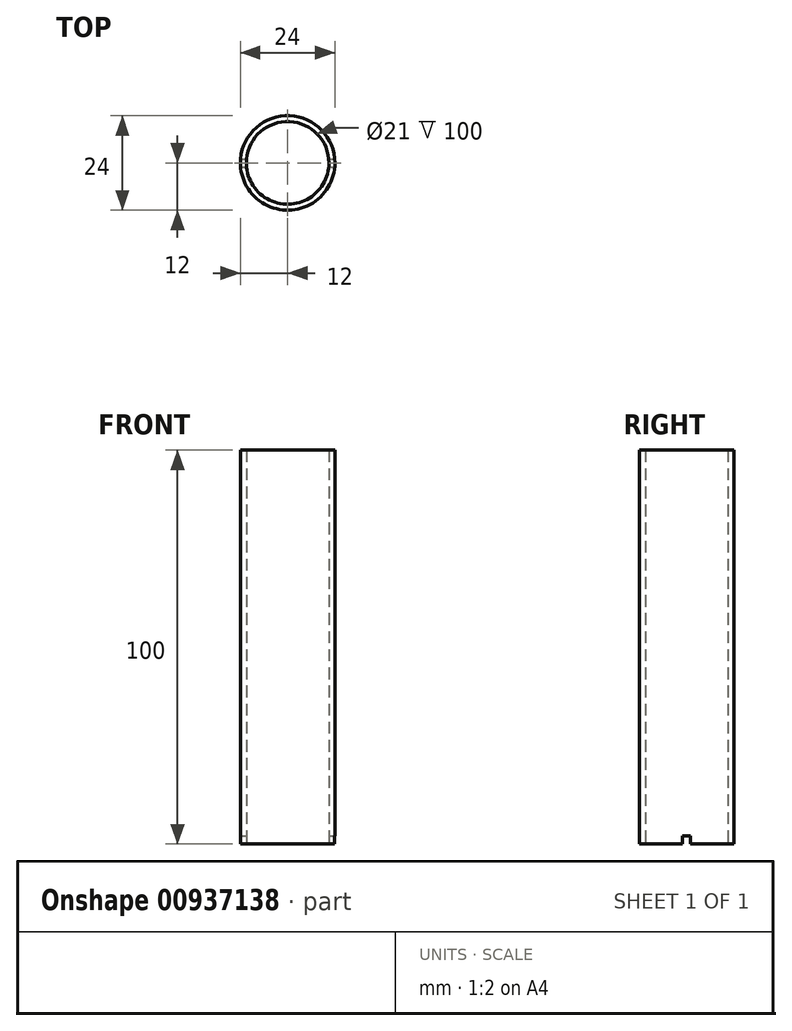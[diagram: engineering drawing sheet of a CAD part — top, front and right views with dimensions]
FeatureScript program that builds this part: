
annotation { "Feature Type Name" : "Feature", "Feature Type Description" : "" }
export const myFeature = defineFeature(function(context is Context, id is Id, definition is map)
    precondition{}
    {
        {
            var Q0;
            Q0=qCreatedBy(makeId("Top.planeOp"),FACE);
            var sketch = newSketch(context, id + "F0", { "sketchPlane" : qUnion([Q0])});
            skCircle(sketch, "E0", {"center": v(0, 0) * mm, "radius": 12 * mm});
            skCircle(sketch, "E1", {"center": v(0, 0) * mm, "radius": 10.5 * mm});
            skSolve(sketch);
        }
        {
            var Q0;
            Q0 = qSketchRegion(id + "F0", true);
            extrude(context, id + "F1", {"entities" : qUnion([Q0]), "depth" : 100 * mm, "offsetDistance" : 25 * mm});
        }
        {
            var Q0;
            Q0=qCreatedBy(makeId("Right.planeOp"),FACE);
            var sketch = newSketch(context, id + "F2", { "sketchPlane" : qUnion([Q0])});
            skLineSegment(sketch, "E2", {"start": v(-1, 0) * mm, "end": v(-1, 2) * mm});
            skLineSegment(sketch, "E3", {"start": v(-1, 2) * mm, "end": v(1, 2) * mm});
            skLineSegment(sketch, "E4", {"start": v(1, 2) * mm, "end": v(1, 0) * mm});
            skLineSegment(sketch, "E5", {"start": v(1, 0) * mm, "end": v(-1, 0) * mm});
            skSolve(sketch);
        }
        {
            var Q0;
            Q0 = qSketchRegion(id + "F2", true);
            extrude(context, id + "F3", {"entities" : qUnion([Q0]), "operationType" : NewBodyOperationType.REMOVE, "endBound" : BoundingType.SYMMETRIC, "oppositeDirection" : true, "depth" : 31.12 * mm, "offsetDistance" : 25 * mm});
        }
    });
